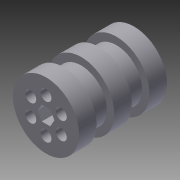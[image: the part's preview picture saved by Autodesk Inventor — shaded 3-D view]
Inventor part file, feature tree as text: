
AUTODESK INVENTOR PART (.ipt)
format: ipt  version: 2012 (Build 160160000, 160)  size: 138,752 bytes
history: native  units: in
note: dims shown in document units (in); Inventor stores cm internally (conversion verified against a paired STEP export)
features: plane x5, sketch x4, extrude x3, hole x1
ambient origin geometry x8: Origin, YZ Plane, XZ Plane, XY Plane, X Axis, Y Axis, Z Axis, Center Point
bodies: Solid1 (feature_tree)
feature tree (13):
  extrude  "Extrusion1"  Depth=1.5in TaperAngle=0.0deg
  plane  "Work Plane5"
  extrude  "Extrusion2"  [1 undecoded]
  sketch  "Sketch3"  dims[d6=-0.3in d7=-0.3in d8=-0.3in]
  hole  "Hole1"  [1 undecoded]
  extrude  "Extrusion4"  Depth=0.3in TaperAngle=0.0deg
  sketch  "Sketch1"  dims[d1=0.25in d2=1.5in d3=0.0in]
  plane  "Work Plane1"
  plane  "Work Plane2"
  plane  "Work Plane3"
  plane  "Work Plane4"
  sketch  "Sketch2"  dims[d4=1.125in d5=-0.3in]
  sketch  "Sketch4"  dims[d9=0.875in d10=0.3in d11=0.0in d15=0.3in d16=2.3622in d18=360.0deg d20=0.1875in d21=0.75in d22=0.375in d23=0.25in d24=0.5635in d25=1.0in d26=0.8108in d27=0.3in d28=0.0in]
note: 2 required parameter values undecoded (feature->parameter linkage not recoverable at this tier; creation-order binding heuristic only, values carry confidence <= 0.55)
